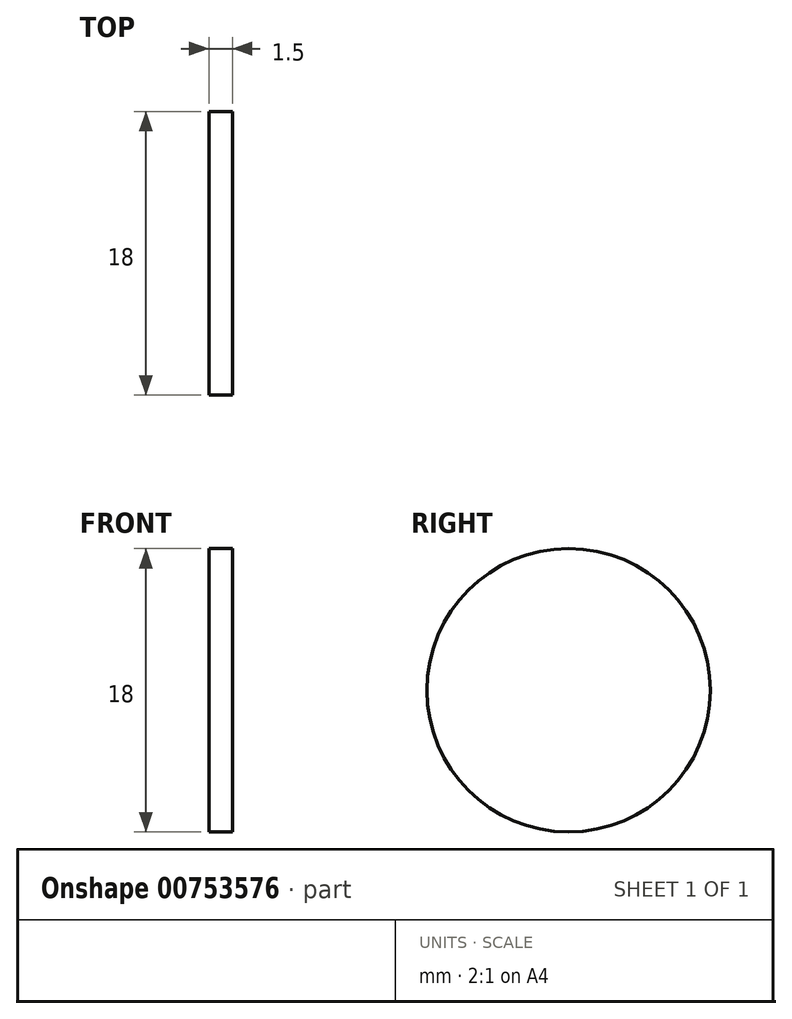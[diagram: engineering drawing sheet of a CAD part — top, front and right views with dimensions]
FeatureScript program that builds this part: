
annotation { "Feature Type Name" : "Feature", "Feature Type Description" : "" }
export const myFeature = defineFeature(function(context is Context, id is Id, definition is map)
    precondition{}
    {
        {
            var Q0;
            Q0=qCreatedBy(makeId("Right.planeOp"),FACE);
            var sketch = newSketch(context, id + "F0", { "sketchPlane" : qUnion([Q0])});
            skCircle(sketch, "E0", {"center": v(0, 0) * mm, "radius": 9 * mm});
            skSolve(sketch);
        }
        {
            var Q0;
            Q0=makeQuery(id+"F0.imprint","IMPRINT",FACE,{"disambiguationData":[TD([[makeQuery(id+"F0.imprint","IMPRINT",EDGE,{"derivedFrom":sQuery(id+"F0.wireOp",EDGE,"E0")}),1.0]])]});
            extrude(context, id + "F1", {"entities" : qUnion([Q0]), "depth" : 1.5 * mm, "offsetDistance" : 25.4 * mm});
        }
    });
